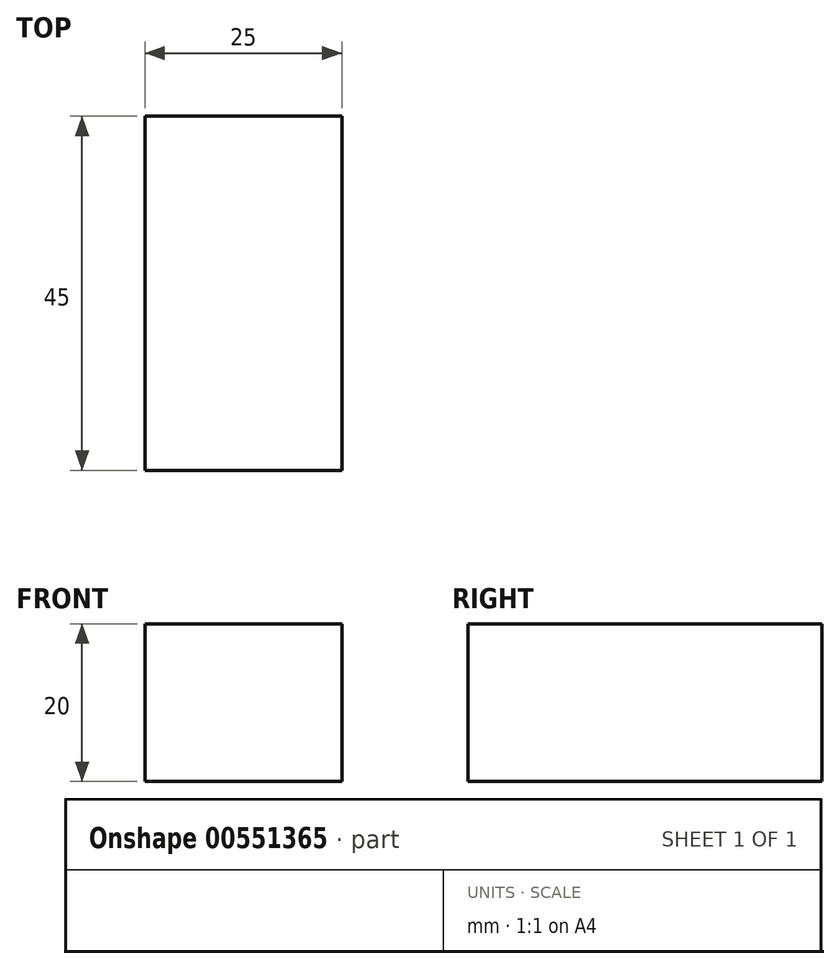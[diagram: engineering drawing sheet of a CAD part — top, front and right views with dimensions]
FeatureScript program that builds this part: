
annotation { "Feature Type Name" : "Feature", "Feature Type Description" : "" }
export const myFeature = defineFeature(function(context is Context, id is Id, definition is map)
    precondition{}
    {
        {
            var Q0;
            Q0=qCreatedBy(makeId("Right.planeOp"),FACE);
            var sketch = newSketch(context, id + "F0", { "sketchPlane" : qUnion([Q0])});
            skLineSegment(sketch, "E0.bottom", {"start": v(-32.67, 22.88) * mm, "end": v(12.33, 22.88) * mm});
            skLineSegment(sketch, "E0.top", {"start": v(-32.67, 2.88) * mm, "end": v(12.33, 2.88) * mm});
            skLineSegment(sketch, "E0.left", {"start": v(-32.67, 22.88) * mm, "end": v(-32.67, 2.88) * mm});
            skLineSegment(sketch, "E0.right", {"start": v(12.33, 22.88) * mm, "end": v(12.33, 2.88) * mm});
            skSolve(sketch);
        }
        {
            var Q0;
            Q0 = qSketchRegion(id + "F0", true);
            extrude(context, id + "F1", {"entities" : qUnion([Q0]), "depth" : 25 * mm, "offsetDistance" : 25 * mm});
        }
    });
